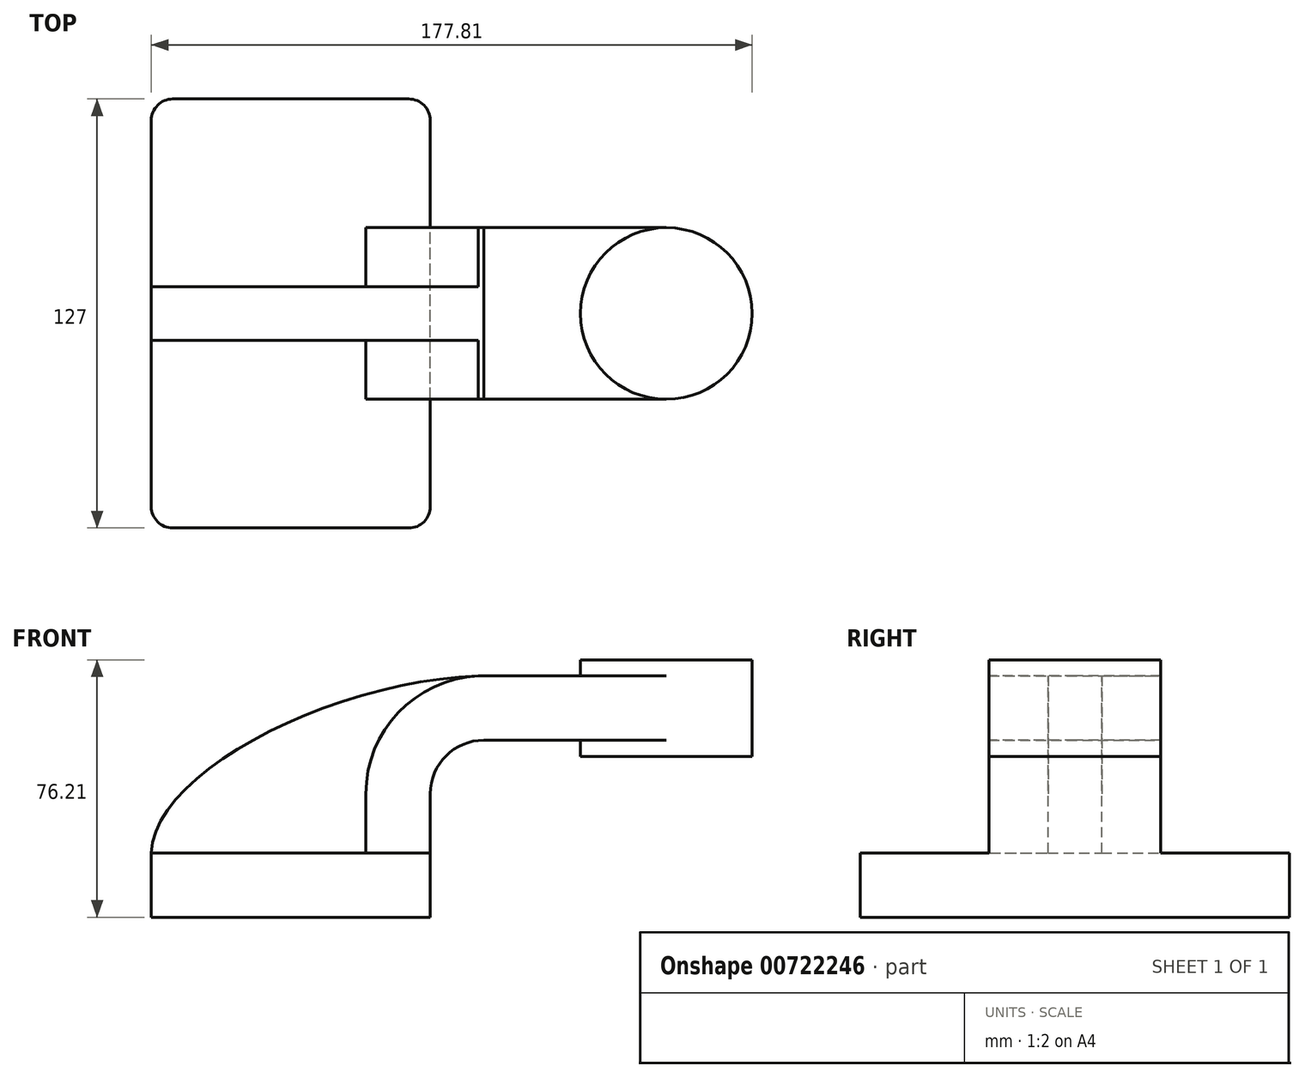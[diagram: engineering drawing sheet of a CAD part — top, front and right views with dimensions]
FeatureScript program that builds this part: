
annotation { "Feature Type Name" : "Feature", "Feature Type Description" : "" }
export const myFeature = defineFeature(function(context is Context, id is Id, definition is map)
    precondition{}
    {
        {
            var Q0;
            Q0=qCreatedBy(makeId("Front.planeOp"),FACE);
            var sketch = newSketch(context, id + "F0", { "sketchPlane" : qUnion([Q0])});
            skLineSegment(sketch, "E0.bottom", {"start": v(-41.28, -9.53) * mm, "end": v(41.28, -9.53) * mm});
            skLineSegment(sketch, "E0.top", {"start": v(-41.28, 9.53) * mm, "end": v(41.28, 9.53) * mm});
            skLineSegment(sketch, "E0.left", {"start": v(-41.27, -9.53) * mm, "end": v(-41.28, 9.53) * mm});
            skLineSegment(sketch, "E0.right", {"start": v(41.28, -9.53) * mm, "end": v(41.28, 9.53) * mm});
            skPoint(sketch, "E0.middle", {"position": v(0, 0) * mm});
            skLineSegment(sketch, "E1.bottom", {"start": v(136.52, 38.1) * mm, "end": v(85.73, 38.1) * mm});
            skLineSegment(sketch, "E1.top", {"start": v(136.52, 66.68) * mm, "end": v(85.72, 66.68) * mm});
            skLineSegment(sketch, "E1.left", {"start": v(136.52, 38.1) * mm, "end": v(136.52, 66.68) * mm});
            skLineSegment(sketch, "E1.right", {"start": v(85.73, 38.1) * mm, "end": v(85.72, 66.68) * mm});
            skPoint(sketch, "E1.middle", {"position": v(111.12, 52.39) * mm});
            skLineSegment(sketch, "E2", {"start": v(41.27, 9.53) * mm, "end": v(41.27, 27) * mm});
            skArc(sketch, "E3", {"start": v(41.27, 27) * mm, "mid": v(45.92, 38.23) * mm, "end": v(57.15, 42.88) * mm});
            skPoint(sketch, "E4.endSnap0", {"position": v(111.12, 38.1) * mm});
            skLineSegment(sketch, "E5", {"start": v(57.15, 42.88) * mm, "end": v(111.13, 42.88) * mm});
            skLineSegment(sketch, "E6.0", {"start": v(57.15, 61.93) * mm, "end": v(111.12, 61.93) * mm});
            skArc(sketch, "E6.1", {"start": v(22.22, 27) * mm, "mid": v(32.45, 51.7) * mm, "end": v(57.15, 61.93) * mm});
            skLineSegment(sketch, "E6.2", {"start": v(22.23, 9.53) * mm, "end": v(22.23, 27) * mm});
            skLineSegment(sketch, "E7", {"start": v(111.13, 38.1) * mm, "end": v(111.12, 66.68) * mm});
            skFitSpline(sketch, "E8", {"points": [v(-41.28, 9.53) * mm, v(57.15, 61.93) * mm], "startDerivative": vector(1.83, 73.27) * mm, "endDerivative": vector(128.76, 2.16) * mm});
            skSolve(sketch);
        }
        {
            var Q0;
            Q0=makeQuery(id+"F0.imprint","IMPRINT",FACE,{"disambiguationData":[TD([[makeQuery(id+"F0.imprint","IMPRINT",EDGE,{"derivedFrom":sQuery(id+"F0.wireOp",EDGE,"E0.bottom")}),1.0]])]});
            extrude(context, id + "F1", {"entities" : qUnion([Q0]), "endBound" : BoundingType.SYMMETRIC, "depth" : 127 * mm, "offsetDistance" : 25.4 * mm});
        }
        {
            var Q0;
            {var subQ1=sQuery(id+"F0.wireOp",EDGE,"E2");Q0=makeQuery(id+"F0.imprint","IMPRINT",FACE,{"disambiguationData":[TD([[makeQuery(id+"F0.imprint","IMPRINT",EDGE,{"derivedFrom":subQ1}),1.0]])]});}
            var Q1;
            {var subQ0=sQuery(id+"F0.wireOp",EDGE,"E5");var subQ1=sQuery(id+"F0.wireOp",EDGE,"E1.right");var subQ2=makeQuery(id+"F0.imprint","INTERSECT",VERTEX,{"derivedFrom":[subQ1,subQ0]});Q1=makeQuery(id+"F0.imprint","IMPRINT",FACE,{"disambiguationData":[TD([[makeQuery(id+"F0.imprint","IMPRINT",EDGE,{"disambiguationData":[TD([[subQ2,-1.0]])],"derivedFrom":subQ1}),-1.0]])]});}
            extrude(context, id + "F2", {"entities" : qUnion([Q0, Q1]), "operationType" : NewBodyOperationType.ADD, "endBound" : BoundingType.SYMMETRIC, "depth" : 50.8 * mm, "offsetDistance" : 25.4 * mm});
        }
        {
            var Q0;
            {var subQ3=sQuery(id+"F0.wireOp",EDGE,"E6.2");Q0=makeQuery(id+"F0.imprint","IMPRINT",FACE,{"disambiguationData":[TD([[makeQuery(id+"F0.imprint","IMPRINT",EDGE,{"derivedFrom":subQ3}),1.0]])]});}
            extrude(context, id + "F3", {"entities" : qUnion([Q0]), "operationType" : NewBodyOperationType.ADD, "endBound" : BoundingType.SYMMETRIC, "depth" : 15.88 * mm, "offsetDistance" : 25.4 * mm});
        }
        {
            var Q0;
            {var subQ0=sQuery(id+"F0.wireOp",EDGE,"E1.left");Q0=makeQuery(id+"F0.imprint","IMPRINT",FACE,{"disambiguationData":[TD([[makeQuery(id+"F0.imprint","IMPRINT",EDGE,{"derivedFrom":subQ0}),1.0]])]});}
            var Q1;
            Q1=sQuery(id+"F0.wireOp",EDGE,"E7");
            revolve(context, id + "F4", {"operationType" : NewBodyOperationType.ADD, "surfaceOperationType" : NewSurfaceOperationType.NEW, "entities" : qUnion([Q0]), "axis" : qUnion([Q1]), "revolveType" : RevolveType.FULL});
        }
        {
            var Q0;
            Q0=makeQuery(id+"F1.opExtrude","CAP_EDGE",EDGE,{"disambiguationData":[OSD([sQuery(id+"F0.wireOp",EDGE,"E0.right")])],"isStart":false});
            var Q1;
            Q1=makeQuery(id+"F1.opExtrude","CAP_EDGE",EDGE,{"disambiguationData":[OSD([sQuery(id+"F0.wireOp",EDGE,"E0.left")])],"isStart":false});
            var Q2;
            Q2=makeQuery(id+"F1.opExtrude","CAP_EDGE",EDGE,{"disambiguationData":[OSD([sQuery(id+"F0.wireOp",EDGE,"E0.right")])],"isStart":true});
            var Q3;
            Q3=makeQuery(id+"F1.opExtrude","CAP_EDGE",EDGE,{"disambiguationData":[OSD([sQuery(id+"F0.wireOp",EDGE,"E0.left")])],"isStart":true});
            fillet(context, id + "F5", {"entities" : qUnion([Q0, Q1, Q2, Q3]), "radius" : 6.35 * mm, "tangentPropagation" : true, "allowEdgeOverflow" : false});
        }
    });
